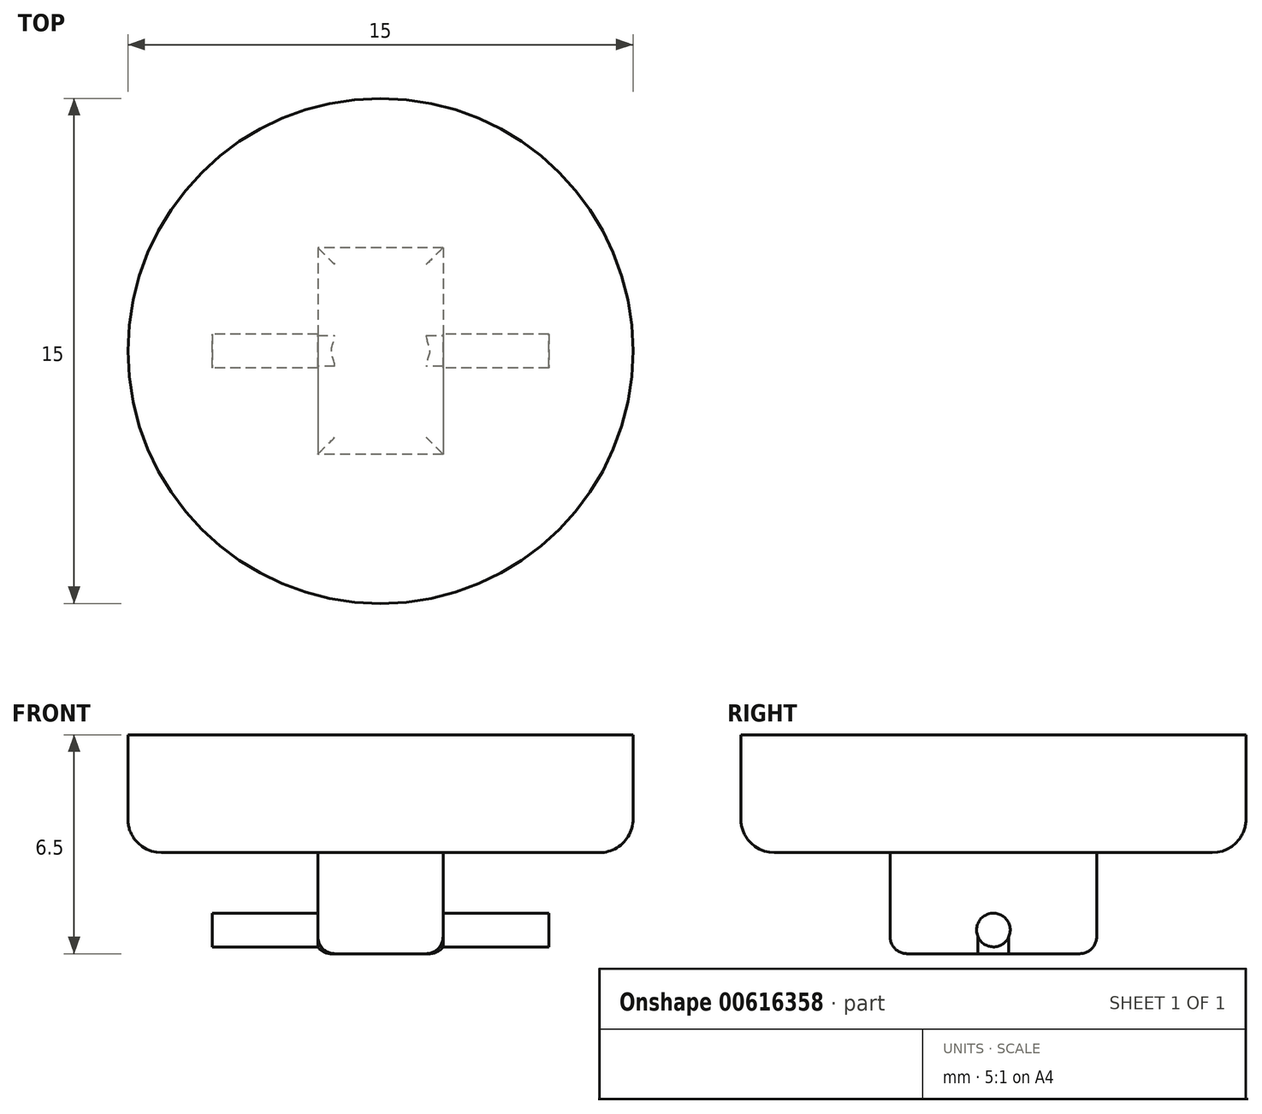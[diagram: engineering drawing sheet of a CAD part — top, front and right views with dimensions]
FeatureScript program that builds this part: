
annotation { "Feature Type Name" : "Feature", "Feature Type Description" : "" }
export const myFeature = defineFeature(function(context is Context, id is Id, definition is map)
    precondition{}
    {
        {
            var Q0;
            Q0=qCreatedBy(makeId("Top.planeOp"),FACE);
            var sketch = newSketch(context, id + "F0", { "sketchPlane" : qUnion([Q0])});
            skCircle(sketch, "E0", {"center": v(0, 0) * mm, "radius": 7.5 * mm});
            skSolve(sketch);
        }
        {
            var Q0;
            Q0 = qSketchRegion(id + "F0", true);
            extrude(context, id + "F1", {"entities" : qUnion([Q0]), "oppositeDirection" : true, "depth" : 3.5 * mm, "offsetDistance" : 25 * mm});
        }
        {
            var Q0;
            Q0=makeQuery(id+"F1.opExtrude","CAP_FACE",FACE,{"disambiguationData":[OSD([sQuery(id+"F0.wireOp",EDGE,"E0")])],"isStart":false});
            var sketch = newSketch(context, id + "F2", { "sketchPlane" : qUnion([Q0])});
            skLineSegment(sketch, "E1.bottom", {"start": v(1.86, -3.07) * mm, "end": v(-1.86, -3.07) * mm});
            skLineSegment(sketch, "E1.top", {"start": v(1.86, 3.07) * mm, "end": v(-1.86, 3.07) * mm});
            skLineSegment(sketch, "E1.left", {"start": v(1.86, -3.07) * mm, "end": v(1.86, 3.07) * mm});
            skLineSegment(sketch, "E1.right", {"start": v(-1.86, -3.07) * mm, "end": v(-1.86, 3.07) * mm});
            skPoint(sketch, "E1.middle", {"position": v(0, 0) * mm});
            skSolve(sketch);
        }
        {
            var Q0;
            Q0 = qSketchRegion(id + "F2", true);
            extrude(context, id + "F3", {"entities" : qUnion([Q0]), "operationType" : NewBodyOperationType.ADD, "depth" : 3 * mm, "offsetDistance" : 25 * mm});
        }
        {
            var Q0;
            Q0=qCreatedBy(makeId("Right.planeOp"),FACE);
            var sketch = newSketch(context, id + "F4", { "sketchPlane" : qUnion([Q0])});
            skCircle(sketch, "E2", {"center": v(0, -5.8) * mm, "radius": 0.5 * mm});
            skSolve(sketch);
        }
        {
            var Q0;
            Q0 = qSketchRegion(id + "F4", true);
            extrude(context, id + "F5", {"entities" : qUnion([Q0]), "operationType" : NewBodyOperationType.ADD, "depth" : 10 * mm, "offsetDistance" : 25 * mm, "symmetric" : true});
        }
        {
            var Q0;
            Q0=makeQuery(id+"F1.opExtrude","CAP_EDGE",EDGE,{"disambiguationData":[OSD([sQuery(id+"F0.wireOp",EDGE,"E0")])],"isStart":false});
            fillet(context, id + "F6", {"entities" : qUnion([Q0]), "radius" : 1 * mm, "tangentPropagation" : true, "allowEdgeOverflow" : false});
        }
        {
            var Q0;
            Q0=makeQuery(id+"F3.opExtrude","CAP_FACE",FACE,{"disambiguationData":[OSD([sQuery(id+"F2.wireOp",EDGE,"E1.bottom"),sQuery(id+"F2.wireOp",EDGE,"E1.top"),sQuery(id+"F2.wireOp",EDGE,"E1.left"),sQuery(id+"F2.wireOp",EDGE,"E1.right")])],"isStart":false});
            fillet(context, id + "F7", {"entities" : qUnion([Q0]), "radius" : 0.5 * mm, "tangentPropagation" : true, "allowEdgeOverflow" : false});
        }
    });
